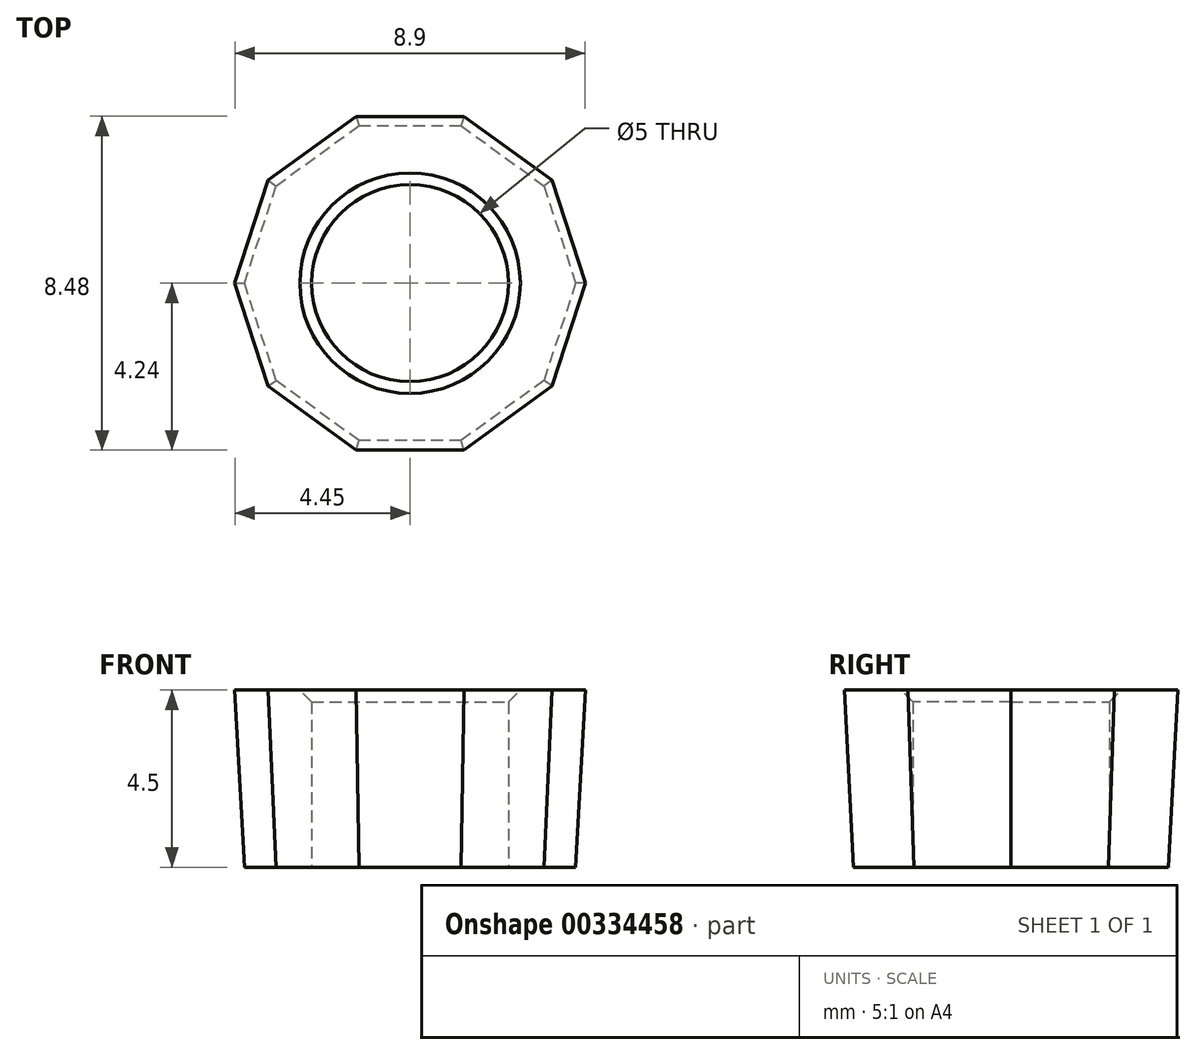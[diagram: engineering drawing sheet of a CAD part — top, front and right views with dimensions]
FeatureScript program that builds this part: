
annotation { "Feature Type Name" : "Feature", "Feature Type Description" : "" }
export const myFeature = defineFeature(function(context is Context, id is Id, definition is map)
    precondition{}
    {
        {
            var Q0;
            Q0=qCreatedBy(makeId("Top.planeOp"),FACE);
            var sketch = newSketch(context, id + "F0", { "sketchPlane" : qUnion([Q0])});
            skCircle(sketch, "E0.cCircle", {"center": v(0, 0) * mm, "radius": 4 * mm, "construction": true});
            skLineSegment(sketch, "E0.0", {"start": v(1.3, -4) * mm, "end": v(-1.3, -4) * mm});
            skLineSegment(sketch, "E0.1", {"start": v(-1.3, -4) * mm, "end": v(-3.4, -2.47) * mm});
            skLineSegment(sketch, "E0.2", {"start": v(-3.4, -2.47) * mm, "end": v(-4.2, 0) * mm});
            skLineSegment(sketch, "E0.3", {"start": v(-4.2, 0) * mm, "end": v(-3.4, 2.47) * mm});
            skLineSegment(sketch, "E0.4", {"start": v(-3.4, 2.47) * mm, "end": v(-1.3, 4) * mm});
            skLineSegment(sketch, "E0.5", {"start": v(-1.3, 4) * mm, "end": v(1.3, 4) * mm});
            skLineSegment(sketch, "E0.6", {"start": v(1.3, 4) * mm, "end": v(3.4, 2.47) * mm});
            skLineSegment(sketch, "E0.7", {"start": v(3.4, 2.47) * mm, "end": v(4.2, 0) * mm});
            skLineSegment(sketch, "E0.8", {"start": v(4.2, 0) * mm, "end": v(3.4, -2.47) * mm});
            skLineSegment(sketch, "E0.9", {"start": v(3.4, -2.47) * mm, "end": v(1.3, -4) * mm});
            skPoint(sketch, "E0.0.midPoint", {"position": v(0, -4) * mm});
            skSolve(sketch);
        }
        {
            var Q0;
            Q0=makeQuery(id+"F0.imprint","IMPRINT",FACE,{"disambiguationData":[TD([[makeQuery(id+"F0.imprint","IMPRINT",EDGE,{"derivedFrom":sQuery(id+"F0.wireOp",EDGE,"E0.0")}),-1.0]])]});
            extrude(context, id + "F1", {"entities" : qUnion([Q0]), "depth" : 4.5 * mm, "hasDraft" : true, "draftAngle" : 3 * degree});
        }
        {
            var Q0;
            Q0=makeQuery(id+"F1.opExtrude","CAP_FACE",FACE,{"disambiguationData":[OSD([sQuery(id+"F0.wireOp",EDGE,"E0.0"),sQuery(id+"F0.wireOp",EDGE,"E0.1"),sQuery(id+"F0.wireOp",EDGE,"E0.2"),sQuery(id+"F0.wireOp",EDGE,"E0.3"),sQuery(id+"F0.wireOp",EDGE,"E0.4"),sQuery(id+"F0.wireOp",EDGE,"E0.5"),sQuery(id+"F0.wireOp",EDGE,"E0.6"),sQuery(id+"F0.wireOp",EDGE,"E0.7"),sQuery(id+"F0.wireOp",EDGE,"E0.8"),sQuery(id+"F0.wireOp",EDGE,"E0.9")])],"isStart":true});
            var sketch = newSketch(context, id + "F2", { "sketchPlane" : qUnion([Q0])});
            skCircle(sketch, "E1", {"center": v(0, 0) * mm, "radius": 2.5 * mm});
            skSolve(sketch);
        }
        {
            var Q0;
            Q0=makeQuery(id+"F2.imprint","IMPRINT",FACE,{"disambiguationData":[TD([[makeQuery(id+"F2.imprint","IMPRINT",EDGE,{"derivedFrom":sQuery(id+"F2.wireOp",EDGE,"E1")}),1.0]])]});
            extrude(context, id + "F3", {"entities" : qUnion([Q0]), "operationType" : NewBodyOperationType.REMOVE, "oppositeDirection" : true, "depth" : 25 * mm});
        }
        {
            var Q0;
            Q0=makeQuery(id+"F3.boolean.opBoolean","COPY",EDGE,{"derivedFrom":makeQuery(id+"F3.opExtrude","CAP_EDGE",EDGE,{"disambiguationData":[OSD([sQuery(id+"F2.wireOp",EDGE,"E1")])],"isStart":true})});
            var Q1;
            Q1=makeQuery(id+"F3.boolean.opBoolean","INTERSECT",EDGE,{"derivedFrom":[makeQuery(id+"F1.opExtrude","CAP_FACE",FACE,{"disambiguationData":[OSD([sQuery(id+"F0.wireOp",EDGE,"E0.0"),sQuery(id+"F0.wireOp",EDGE,"E0.1"),sQuery(id+"F0.wireOp",EDGE,"E0.2"),sQuery(id+"F0.wireOp",EDGE,"E0.3"),sQuery(id+"F0.wireOp",EDGE,"E0.4"),sQuery(id+"F0.wireOp",EDGE,"E0.5"),sQuery(id+"F0.wireOp",EDGE,"E0.6"),sQuery(id+"F0.wireOp",EDGE,"E0.7"),sQuery(id+"F0.wireOp",EDGE,"E0.8"),sQuery(id+"F0.wireOp",EDGE,"E0.9")])],"isStart":false}),makeQuery(id+"F3.opExtrude","SWEPT_FACE",FACE,{"disambiguationData":[OSD([sQuery(id+"F2.wireOp",EDGE,"E1")])]})]});
            chamfer(context, id + "F4", {"entities" : qUnion([Q0, Q1]), "width" : 0.3 * mm, "tangentPropagation" : true});
        }
    });
